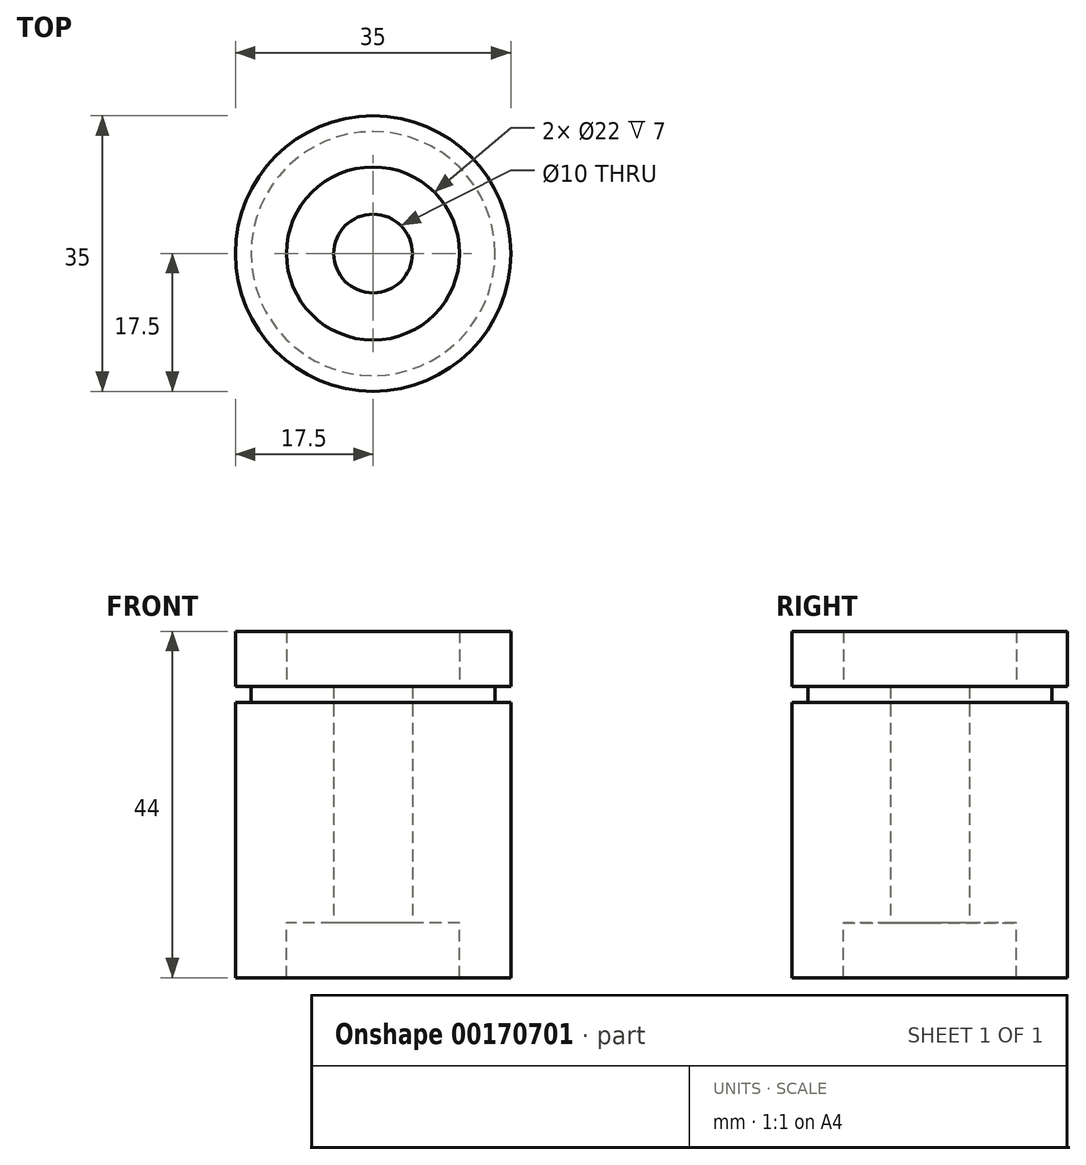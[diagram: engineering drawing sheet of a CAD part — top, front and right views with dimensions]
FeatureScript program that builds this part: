
annotation { "Feature Type Name" : "Feature", "Feature Type Description" : "" }
export const myFeature = defineFeature(function(context is Context, id is Id, definition is map)
    precondition{}
    {
        {
            var Q0;
            Q0=qCreatedBy(makeId("Top.planeOp"),FACE);
            var sketch = newSketch(context, id + "F0", { "sketchPlane" : qUnion([Q0])});
            skCircle(sketch, "E0", {"center": v(0, 0) * mm, "radius": 5 * mm});
            skCircle(sketch, "E1", {"center": v(0, 0) * mm, "radius": 17.5 * mm});
            skSolve(sketch);
        }
        {
            var Q0;
            Q0=makeQuery(id+"F0.imprint","IMPRINT",FACE,{"disambiguationData":[TD([[makeQuery(id+"F0.imprint","IMPRINT",EDGE,{"derivedFrom":sQuery(id+"F0.wireOp",EDGE,"E0")}),-1.0]])]});
            extrude(context, id + "F1", {"entities" : qUnion([Q0]), "depth" : 15 * mm});
        }
        {
            var Q0;
            Q0=makeQuery(id+"F1.opExtrude","CAP_FACE",FACE,{"disambiguationData":[OSD([sQuery(id+"F0.wireOp",EDGE,"E0"),sQuery(id+"F0.wireOp",EDGE,"E1")])],"isStart":false});
            var sketch = newSketch(context, id + "F2", { "sketchPlane" : qUnion([Q0])});
            skCircle(sketch, "E2", {"center": v(0, 0) * mm, "radius": 17.5 * mm});
            skCircle(sketch, "E3", {"center": v(0, 0) * mm, "radius": 11 * mm});
            skSolve(sketch);
        }
        {
            var Q0;
            Q0=makeQuery(id+"F2.imprint","IMPRINT",FACE,{"disambiguationData":[TD([[makeQuery(id+"F2.imprint","IMPRINT",EDGE,{"derivedFrom":sQuery(id+"F2.wireOp",EDGE,"E2")}),1.0]])]});
            extrude(context, id + "F3", {"entities" : qUnion([Q0]), "operationType" : NewBodyOperationType.ADD, "depth" : 7 * mm});
        }
        {
            var Q0;
            Q0=makeQuery(id+"F1.opExtrude","SWEPT_BODY",BODY,{"disambiguationData":[OSD([sQuery(id+"F0.wireOp",EDGE,"E0"),sQuery(id+"F0.wireOp",EDGE,"E1")])]});
            var Q1;
            Q1=qCreatedBy(makeId("Top.planeOp"),FACE);
            mirror(context, id + "F4", {"operationType" : NewBodyOperationType.ADD, "entities" : qUnion([Q0]), "mirrorPlane" : qUnion([Q1])});
        }
        {
            var Q0;
            Q0=qCreatedBy(makeId("Top.planeOp"),FACE);
            cPlane(context, id + "F5", {"entities" : qUnion([Q0]), "cplaneType" : CPlaneType.OFFSET, "offset" : 15 * mm, "width" : 150 * mm, "height" : 150 * mm});
        }
        {
            var Q0;
            Q0=qCreatedBy(id+"F5.planeOp",FACE);
            var sketch = newSketch(context, id + "F6", { "sketchPlane" : qUnion([Q0])});
            skCircle(sketch, "E4", {"center": v(0, 0) * mm, "radius": 17.5 * mm});
            skCircle(sketch, "E5", {"center": v(0, 0) * mm, "radius": 15.5 * mm});
            skSolve(sketch);
        }
        {
            var Q0;
            Q0 = qSketchRegion(id + "F6", true);
            extrude(context, id + "F7", {"entities" : qUnion([Q0]), "operationType" : NewBodyOperationType.REMOVE, "oppositeDirection" : true, "depth" : 2 * mm});
        }
    });
